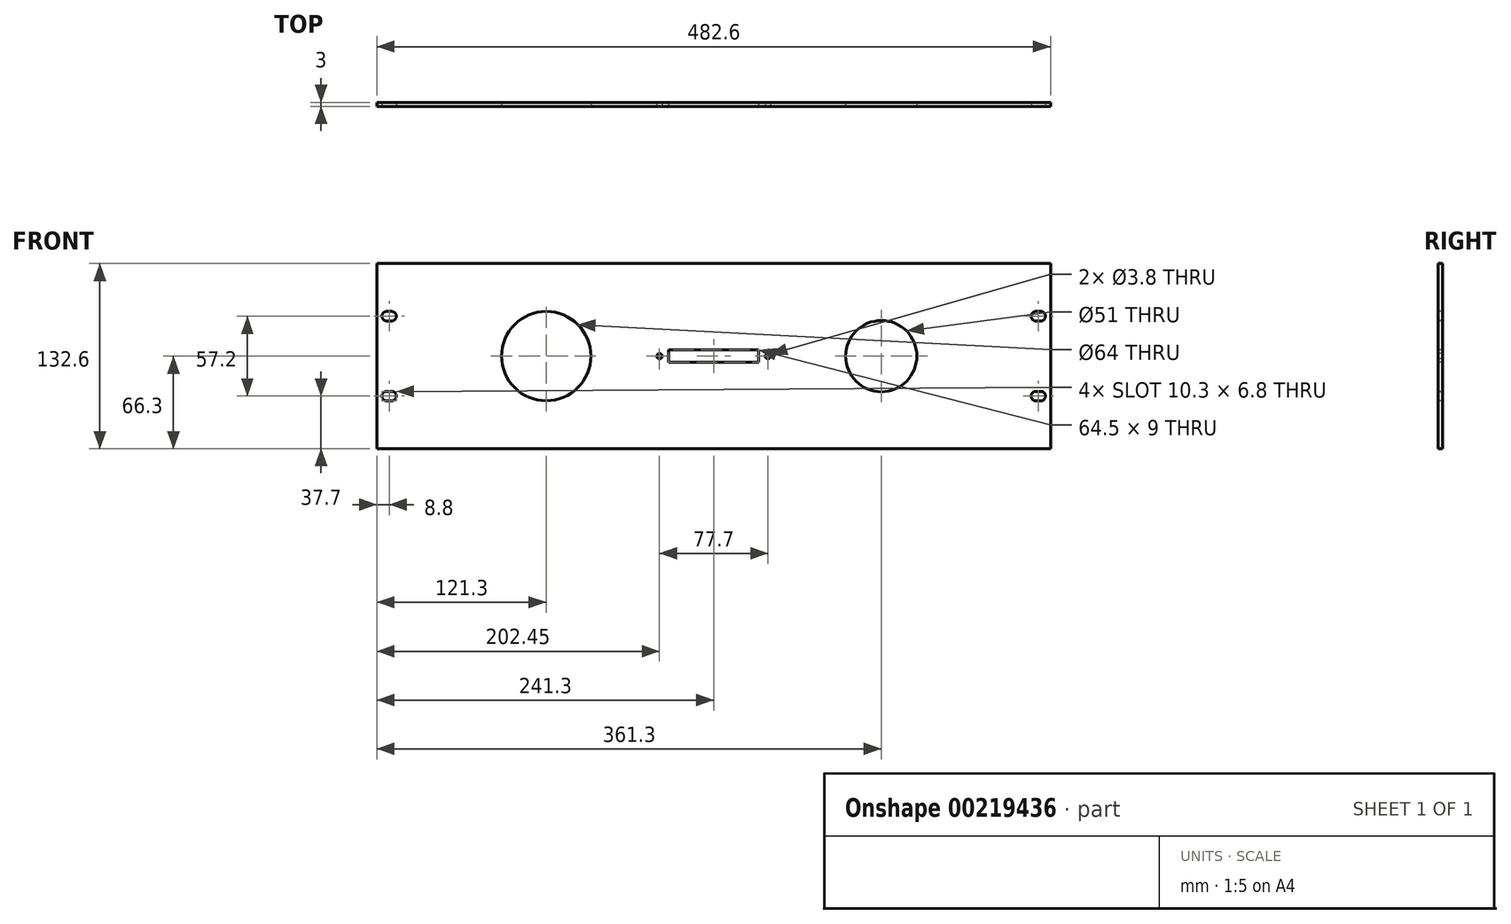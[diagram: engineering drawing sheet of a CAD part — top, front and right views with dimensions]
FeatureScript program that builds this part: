
annotation { "Feature Type Name" : "Feature", "Feature Type Description" : "" }
export const myFeature = defineFeature(function(context is Context, id is Id, definition is map)
    precondition{}
    {
        {
            var Q0;
            Q0=qCreatedBy(makeId("Front.planeOp"),FACE);
            var sketch = newSketch(context, id + "F0", { "sketchPlane" : qUnion([Q0])});
            skLineSegment(sketch, "E0.bottom", {"start": v(-241.3, 66.3) * mm, "end": v(241.3, 66.3) * mm});
            skLineSegment(sketch, "E0.top", {"start": v(-241.3, -66.3) * mm, "end": v(241.3, -66.3) * mm});
            skLineSegment(sketch, "E0.left", {"start": v(-241.3, 66.3) * mm, "end": v(-241.3, -66.3) * mm});
            skLineSegment(sketch, "E0.right", {"start": v(241.3, 66.3) * mm, "end": v(241.3, -66.3) * mm});
            skPoint(sketch, "E0.middle", {"position": v(0, 0) * mm});
            skSolve(sketch);
        }
        {
            var Q0;
            Q0=qSketchRegion(id+"F0",true);
            extrude(context, id + "F1", {"entities" : qUnion([Q0]), "oppositeDirection" : true, "depth" : 3 * mm});
        }
        {
            var Q0;
            Q0=makeQuery(id+"F1.opExtrude","CAP_FACE",FACE,{"disambiguationData":[OSD([sQuery(id+"F0.wireOp",EDGE,"E0.bottom"),sQuery(id+"F0.wireOp",EDGE,"E0.top"),sQuery(id+"F0.wireOp",EDGE,"E0.left"),sQuery(id+"F0.wireOp",EDGE,"E0.right")])],"isStart":true});
            var sketch = newSketch(context, id + "F2", { "sketchPlane" : qUnion([Q0])});
            skLineSegment(sketch, "E1.bottom", {"start": v(-230.75, 25.2) * mm, "end": v(-234.25, 25.2) * mm});
            skLineSegment(sketch, "E1.top", {"start": v(-230.75, 32) * mm, "end": v(-234.25, 32) * mm});
            skLineSegment(sketch, "E1.left", {"start": v(-230.75, 25.2) * mm, "end": v(-230.75, 32) * mm});
            skLineSegment(sketch, "E1.right", {"start": v(-234.25, 25.2) * mm, "end": v(-234.25, 32) * mm});
            skPoint(sketch, "E1.middle", {"position": v(-232.5, 28.6) * mm});
            skArc(sketch, "E2", {"start": v(-230.75, 25.2) * mm, "mid": v(-227.35, 28.6) * mm, "end": v(-230.75, 32) * mm});
            skArc(sketch, "E3", {"start": v(-234.25, 32) * mm, "mid": v(-237.65, 28.6) * mm, "end": v(-234.25, 25.2) * mm});
            skSolve(sketch);
        }
        {
            var Q0;
            Q0=makeQuery(id+"F2.imprint","IMPRINT",FACE,{"disambiguationData":[TD([[makeQuery(id+"F2.imprint","IMPRINT",EDGE,{"derivedFrom":sQuery(id+"F2.wireOp",EDGE,"E1.bottom")}),1.0]])]});
            var sketch = newSketch(context, id + "F3", { "sketchPlane" : qUnion([Q0])});
            skLineSegment(sketch, "E4.bottom", {"start": v(-230.75, -32) * mm, "end": v(-234.25, -32) * mm});
            skLineSegment(sketch, "E4.top", {"start": v(-230.75, -25.2) * mm, "end": v(-234.25, -25.2) * mm});
            skLineSegment(sketch, "E4.left", {"start": v(-230.75, -32) * mm, "end": v(-230.75, -25.2) * mm});
            skLineSegment(sketch, "E4.right", {"start": v(-234.25, -32) * mm, "end": v(-234.25, -25.2) * mm});
            skPoint(sketch, "E4.middle", {"position": v(-232.5, -28.6) * mm});
            skArc(sketch, "E5", {"start": v(-230.75, -32) * mm, "mid": v(-227.35, -28.6) * mm, "end": v(-230.75, -25.2) * mm});
            skArc(sketch, "E6", {"start": v(-234.25, -25.2) * mm, "mid": v(-237.65, -28.6) * mm, "end": v(-234.25, -32) * mm});
            skSolve(sketch);
        }
        {
            var Q0;
            Q0=makeQuery(id+"F2.imprint","IMPRINT",FACE,{"disambiguationData":[TD([[makeQuery(id+"F2.imprint","IMPRINT",EDGE,{"derivedFrom":sQuery(id+"F2.wireOp",EDGE,"E1.bottom")}),1.0]])]});
            var sketch = newSketch(context, id + "F4", { "sketchPlane" : qUnion([Q0])});
            skLineSegment(sketch, "E7.bottom", {"start": v(234.25, 32) * mm, "end": v(230.75, 32) * mm});
            skLineSegment(sketch, "E7.top", {"start": v(234.25, 25.2) * mm, "end": v(230.75, 25.2) * mm});
            skLineSegment(sketch, "E7.left", {"start": v(234.25, 32) * mm, "end": v(234.25, 25.2) * mm});
            skLineSegment(sketch, "E7.right", {"start": v(230.75, 32) * mm, "end": v(230.75, 25.2) * mm});
            skPoint(sketch, "E7.middle", {"position": v(232.5, 28.6) * mm});
            skArc(sketch, "E8", {"start": v(234.25, 25.2) * mm, "mid": v(237.65, 28.6) * mm, "end": v(234.25, 32) * mm});
            skArc(sketch, "E9", {"start": v(230.75, 32) * mm, "mid": v(227.35, 28.6) * mm, "end": v(230.75, 25.2) * mm});
            skSolve(sketch);
        }
        {
            var Q0;
            Q0=makeQuery(id+"F2.imprint","IMPRINT",FACE,{"disambiguationData":[TD([[makeQuery(id+"F2.imprint","IMPRINT",EDGE,{"derivedFrom":sQuery(id+"F2.wireOp",EDGE,"E1.bottom")}),1.0]])]});
            var sketch = newSketch(context, id + "F5", { "sketchPlane" : qUnion([Q0])});
            skLineSegment(sketch, "E10.bottom", {"start": v(234.25, -32) * mm, "end": v(230.75, -32) * mm});
            skLineSegment(sketch, "E10.top", {"start": v(234.25, -25.2) * mm, "end": v(230.75, -25.2) * mm});
            skLineSegment(sketch, "E10.left", {"start": v(234.25, -32) * mm, "end": v(234.25, -25.2) * mm});
            skLineSegment(sketch, "E10.right", {"start": v(230.75, -32) * mm, "end": v(230.75, -25.2) * mm});
            skPoint(sketch, "E10.middle", {"position": v(232.5, -28.6) * mm});
            skArc(sketch, "E11", {"start": v(230.75, -25.2) * mm, "mid": v(227.35, -28.6) * mm, "end": v(230.75, -32) * mm});
            skArc(sketch, "E12", {"start": v(234.25, -32) * mm, "mid": v(237.65, -28.6) * mm, "end": v(234.25, -25.2) * mm});
            skSolve(sketch);
        }
        {
            var Q0;
            Q0=qSketchRegion(id+"F2",true);
            var Q1;
            Q1=qSketchRegion(id+"F3",true);
            var Q2;
            Q2=qSketchRegion(id+"F4",true);
            var Q3;
            Q3=qSketchRegion(id+"F5",true);
            extrude(context, id + "F6", {"entities" : qUnion([Q0, Q1, Q2, Q3]), "operationType" : NewBodyOperationType.REMOVE, "oppositeDirection" : true, "depth" : 3 * mm});
        }
        {
            var Q0;
            Q0=makeQuery(id+"F1.opExtrude","CAP_FACE",FACE,{"disambiguationData":[OSD([sQuery(id+"F0.wireOp",EDGE,"E0.bottom"),sQuery(id+"F0.wireOp",EDGE,"E0.top"),sQuery(id+"F0.wireOp",EDGE,"E0.left"),sQuery(id+"F0.wireOp",EDGE,"E0.right")])],"isStart":true});
            var sketch = newSketch(context, id + "F7", { "sketchPlane" : qUnion([Q0])});
            skCircle(sketch, "E13", {"center": v(-120, 0) * mm, "radius": 32 * mm});
            skCircle(sketch, "E14", {"center": v(120, 0) * mm, "radius": 25.5 * mm});
            skLineSegment(sketch, "E15.bottom", {"start": v(-32.25, 4.5) * mm, "end": v(32.25, 4.5) * mm});
            skLineSegment(sketch, "E15.top", {"start": v(-32.25, -4.5) * mm, "end": v(32.25, -4.5) * mm});
            skLineSegment(sketch, "E15.left", {"start": v(-32.25, 4.5) * mm, "end": v(-32.25, -4.5) * mm});
            skLineSegment(sketch, "E15.right", {"start": v(32.25, 4.5) * mm, "end": v(32.25, -4.5) * mm});
            skCircle(sketch, "E16", {"center": v(38.85, 0) * mm, "radius": 1.9 * mm});
            skCircle(sketch, "E17", {"center": v(-38.85, 0) * mm, "radius": 1.9 * mm});
            skSolve(sketch);
        }
        {
            var Q0;
            Q0=qSketchRegion(id+"F7",true);
            extrude(context, id + "F8", {"entities" : qUnion([Q0]), "operationType" : NewBodyOperationType.REMOVE, "oppositeDirection" : true, "depth" : 3 * mm});
        }
    });
